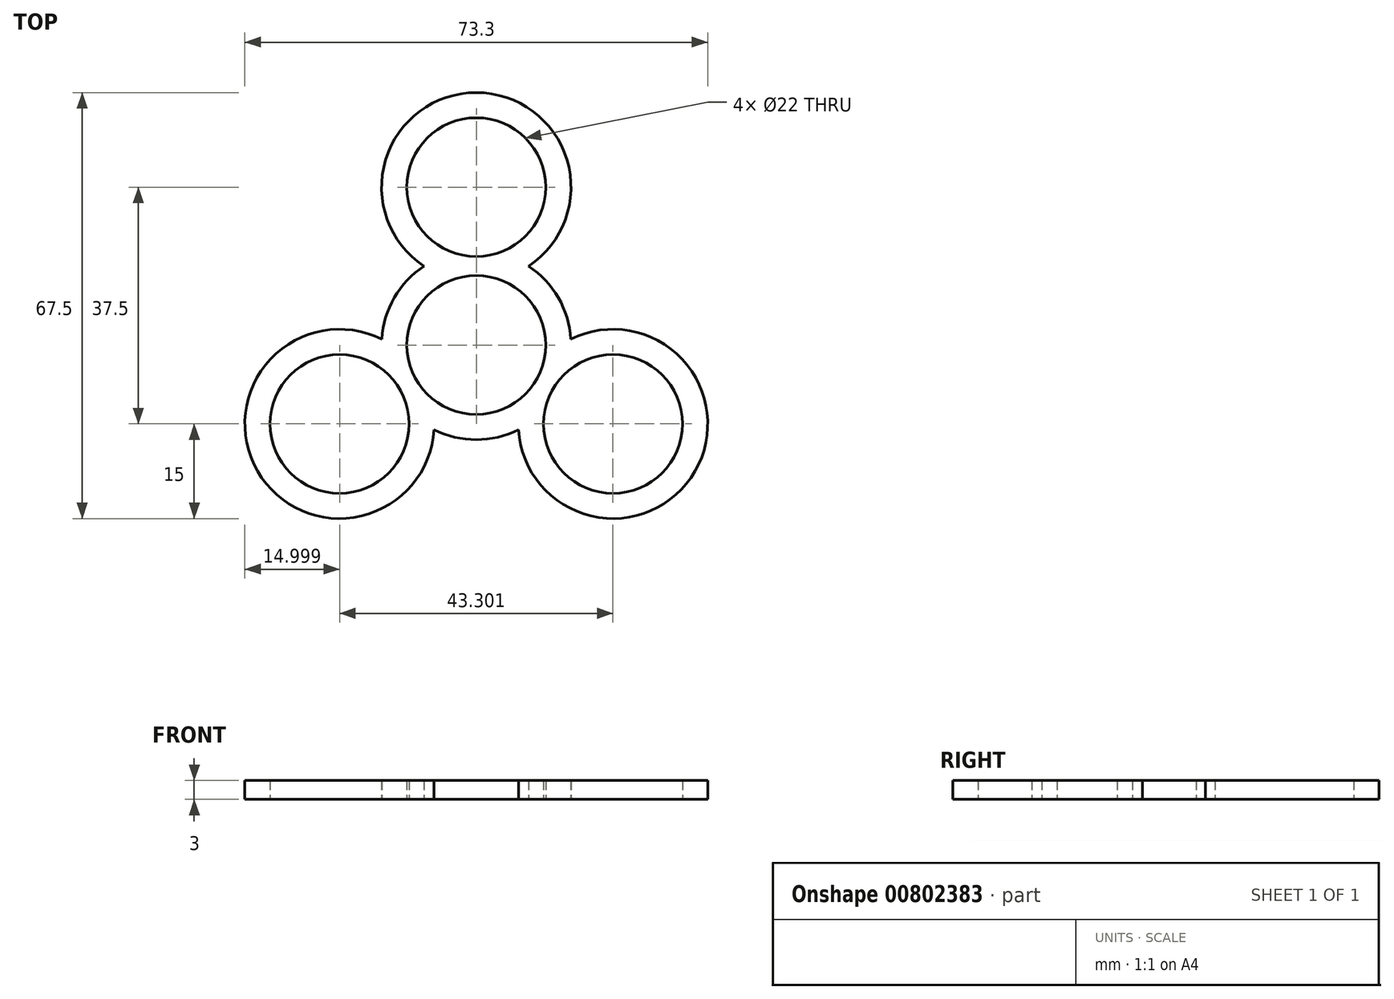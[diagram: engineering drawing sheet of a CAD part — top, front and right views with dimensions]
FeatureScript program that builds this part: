
annotation { "Feature Type Name" : "Feature", "Feature Type Description" : "" }
export const myFeature = defineFeature(function(context is Context, id is Id, definition is map)
    precondition{}
    {
        {
            var Q0;
            Q0=qCreatedBy(makeId("Top.planeOp"),FACE);
            var sketch = newSketch(context, id + "F0", { "sketchPlane" : qUnion([Q0])});
            skArc(sketch, "E0", {"start": v(9.53, 5.5) * mm, "mid": v(0, 11) * mm, "end": v(-9.53, 5.5) * mm});
            skCircle(sketch, "E1", {"center": v(0, 25) * mm, "radius": 11 * mm});
            skArc(sketch, "E2", {"start": v(8.3, 12.5) * mm, "mid": v(0, 40) * mm, "end": v(-8.3, 12.5) * mm});
            skArc(sketch, "E3", {"start": v(-8.3, 12.5) * mm, "mid": v(-10.93, 10.27) * mm, "end": v(-13, 7.5) * mm});
            skArc(sketch, "E4.trimOffspring", {"start": v(13, 7.5) * mm, "mid": v(10.93, 10.27) * mm, "end": v(8.3, 12.5) * mm});
            skArc(sketch, "E5.1.0", {"start": v(-14.97, 0.93) * mm, "mid": v(-34.64, -20) * mm, "end": v(-6.68, -13.43) * mm});
            skCircle(sketch, "E5.1.1", {"center": v(-21.65, -12.5) * mm, "radius": 11 * mm});
            skArc(sketch, "E5.1.2", {"start": v(-13, 7.5) * mm, "mid": v(-14.36, 4.33) * mm, "end": v(-14.97, 0.93) * mm});
            skArc(sketch, "E5.1.3", {"start": v(-6.68, -13.43) * mm, "mid": v(-3.43, -14.6) * mm, "end": v(0, -15) * mm});
            skArc(sketch, "E5.1.4", {"start": v(-9.53, 5.5) * mm, "mid": v(-9.53, -5.5) * mm, "end": v(0, -11) * mm});
            skArc(sketch, "E5.2.0", {"start": v(6.68, -13.43) * mm, "mid": v(34.64, -20) * mm, "end": v(14.97, 0.93) * mm});
            skCircle(sketch, "E5.2.1", {"center": v(21.65, -12.5) * mm, "radius": 11 * mm});
            skArc(sketch, "E5.2.2", {"start": v(0, -15) * mm, "mid": v(3.43, -14.6) * mm, "end": v(6.68, -13.43) * mm});
            skArc(sketch, "E5.2.3", {"start": v(14.97, 0.93) * mm, "mid": v(14.36, 4.33) * mm, "end": v(13, 7.5) * mm});
            skArc(sketch, "E5.2.4", {"start": v(0, -11) * mm, "mid": v(9.53, -5.5) * mm, "end": v(9.53, 5.5) * mm});
            skSolve(sketch);
        }
        {
            var Q0;
            Q0 = qSketchRegion(id + "F0", true);
            extrude(context, id + "F1", {"entities" : qUnion([Q0]), "depth" : 3 * mm, "offsetDistance" : 25 * mm});
        }
    });
